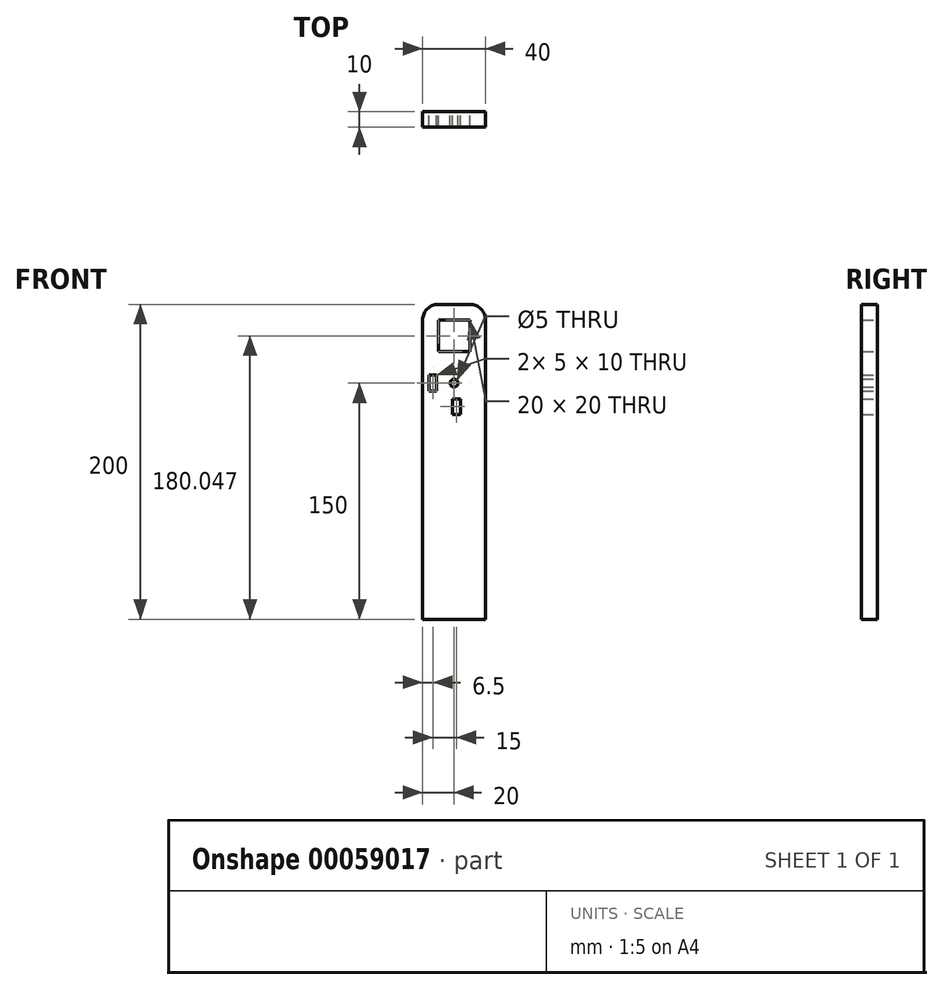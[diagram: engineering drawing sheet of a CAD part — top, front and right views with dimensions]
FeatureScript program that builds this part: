
annotation { "Feature Type Name" : "Feature", "Feature Type Description" : "" }
export const myFeature = defineFeature(function(context is Context, id is Id, definition is map)
    precondition{}
    {
        {
            var Q0;
            Q0=qCreatedBy(makeId("Front.planeOp"),FACE);
            var sketch = newSketch(context, id + "F0", { "sketchPlane" : qUnion([Q0])});
            skLineSegment(sketch, "E0.rect.bottom", {"start": v(-20, 100) * mm, "end": v(20, 100) * mm});
            skLineSegment(sketch, "E0.rect.top", {"start": v(-20, -100) * mm, "end": v(20, -100) * mm});
            skLineSegment(sketch, "E0.rect.left", {"start": v(-20, 100) * mm, "end": v(-20, -100) * mm});
            skLineSegment(sketch, "E0.rect.right", {"start": v(20, 100) * mm, "end": v(20, -100) * mm});
            skPoint(sketch, "E0.rect.middle", {"position": v(0, 0) * mm});
            skCircle(sketch, "E1", {"center": v(0, 50) * mm, "radius": 2.5 * mm});
            skLineSegment(sketch, "E2.rect.bottom", {"start": v(-1, 40) * mm, "end": v(4, 40) * mm});
            skLineSegment(sketch, "E2.rect.top", {"start": v(-1, 30) * mm, "end": v(4, 30) * mm});
            skLineSegment(sketch, "E2.rect.left", {"start": v(-1, 40) * mm, "end": v(-1, 30) * mm});
            skLineSegment(sketch, "E2.rect.right", {"start": v(4, 40) * mm, "end": v(4, 30) * mm});
            skPoint(sketch, "E2.rect.middle", {"position": v(1.5, 35) * mm});
            skLineSegment(sketch, "E3.rect.bottom", {"start": v(-10, 90.05) * mm, "end": v(10, 90.05) * mm});
            skLineSegment(sketch, "E3.rect.top", {"start": v(-10, 70.05) * mm, "end": v(10, 70.05) * mm});
            skLineSegment(sketch, "E3.rect.left", {"start": v(-10, 90.05) * mm, "end": v(-10, 70.05) * mm});
            skLineSegment(sketch, "E3.rect.right", {"start": v(10, 90.05) * mm, "end": v(10, 70.05) * mm});
            skPoint(sketch, "E3.rect.middle", {"position": v(0, 80.05) * mm});
            skPoint(sketch, "E3.rect.middle.positionSnap0", {"position": v(0, 100) * mm});
            skPoint(sketch, "E3.rect.centerSnap0", {"position": v(0, 100) * mm});
            skLineSegment(sketch, "E4.rect.bottom", {"start": v(-16, 55) * mm, "end": v(-11, 55) * mm});
            skLineSegment(sketch, "E4.rect.top", {"start": v(-16, 45) * mm, "end": v(-11, 45) * mm});
            skLineSegment(sketch, "E4.rect.left", {"start": v(-16, 55) * mm, "end": v(-16, 45) * mm});
            skLineSegment(sketch, "E4.rect.right", {"start": v(-11, 55) * mm, "end": v(-11, 45) * mm});
            skPoint(sketch, "E4.rect.middle", {"position": v(-13.5, 50) * mm});
            skSolve(sketch);
        }
        {
            var Q0;
            Q0 = qSketchRegion(id + "F0", true);
            extrude(context, id + "F1", {"entities" : qUnion([Q0]), "depth" : 10 * mm});
        }
        {
            var Q0;
            Q0=makeQuery(id+"F1.opExtrude","SWEPT_EDGE",EDGE,{"disambiguationData":[OSD([sQuery(id+"F0.wireOp",EDGE,"E0.rect.bottom"),sQuery(id+"F0.wireOp",EDGE,"E0.rect.right")])]});
            var Q1;
            Q1=makeQuery(id+"F1.opExtrude","SWEPT_EDGE",EDGE,{"disambiguationData":[OSD([sQuery(id+"F0.wireOp",EDGE,"E0.rect.bottom"),sQuery(id+"F0.wireOp",EDGE,"E0.rect.left")])]});
            fillet(context, id + "F2", {"entities" : qUnion([Q0, Q1]), "radius" : 10 * mm, "tangentPropagation" : true, "allowEdgeOverflow" : false});
        }
    });
